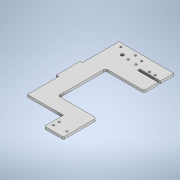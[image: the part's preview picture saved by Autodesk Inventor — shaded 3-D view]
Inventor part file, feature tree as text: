
AUTODESK INVENTOR PART (.ipt)
format: ipt  version: 2021 (Build 250183000, 183)  size: 219,648 bytes
history: native  units: mm
features: sketch x8, extrude x4, hole x4, fillet x2
ambient origin geometry x8: Origin, YZ Plane, XZ Plane, XY Plane, X Axis, Y Axis, Z Axis, Center Point
bodies: Solid1 (feature_tree)
feature tree (18):
  extrude  "Extrusion1"  Depth=77.75mm
  hole  "Hole1"  [1 undecoded]
  fillet  "Fillet1"  Radius=40.0mm
  hole  "Hole2"  [1 undecoded]
  extrude  "Extrusion3"  Depth=31.0mm
  hole  "Hole3"  [1 undecoded]
  hole  "Hole4"  [1 undecoded]
  extrude  "Extrusion4"  Depth=2.0mm
  extrude  "Extrusion5"  Depth=4.0mm
  fillet  "Fillet3"  Radius=12.0mm
  sketch  "Sketch1"  dims[d0=116.2mm d6=77.75mm]
  sketch  "Sketch2"  dims[d8=50.0mm d9=5.0mm d11=40.0mm]
  sketch  "Sketch3"  dims[d12=40.0mm d14=5.0mm d15=0.0mm]
  sketch  "Sketch5"  dims[d16=31.0mm d17=8.0mm]
  sketch  "Sketch6"  dims[d18=12.0mm d19=17.0mm]
  sketch  "Sketch7"  dims[d20=12.0mm d21=8.0mm]
  sketch  "Sketch8"  dims[d22=3.8mm d23=6.0mm d24=4.0mm d25=2.0mm d26=90.0deg d27=8.0mm d28=20.594885mm d29=2.0mm]
  sketch  "Sketch9"  dims[d31=194.0mm d32=60.0mm d33=12.0mm d34=12.0mm d35=3.8mm d36=6.0mm d37=4.0mm d38=2.0mm d39=90.0deg d40=8.0mm d41=20.594885mm d47=44.0mm d48=5.05mm d49=33.3mm d50=2.0mm d51=5.0mm d52=0.0mm d53=23.25mm d54=16.0mm d55=28.0mm d56=73.5mm d57=3.8mm d58=6.0mm d59=4.0mm d60=2.0mm d61=90.0deg d62=8.0mm d63=20.594885mm d64=6.5mm d65=14.0mm d66=3.8mm d67=6.0mm d68=4.0mm d69=2.0mm d70=90.0deg d71=8.0mm d72=20.594885mm d73=21.0mm d74=6.0mm d75=6.0mm d76=25.0mm d77=2.5mm d78=0.0mm d79=0.0mm d80=30.0mm d81=30.0mm d82=35.0mm d83=0.0mm d84=0.0mm d85=4.0mm]
note: 4 required parameter values undecoded (feature->parameter linkage not recoverable at this tier; creation-order binding heuristic only, values carry confidence <= 0.55)
